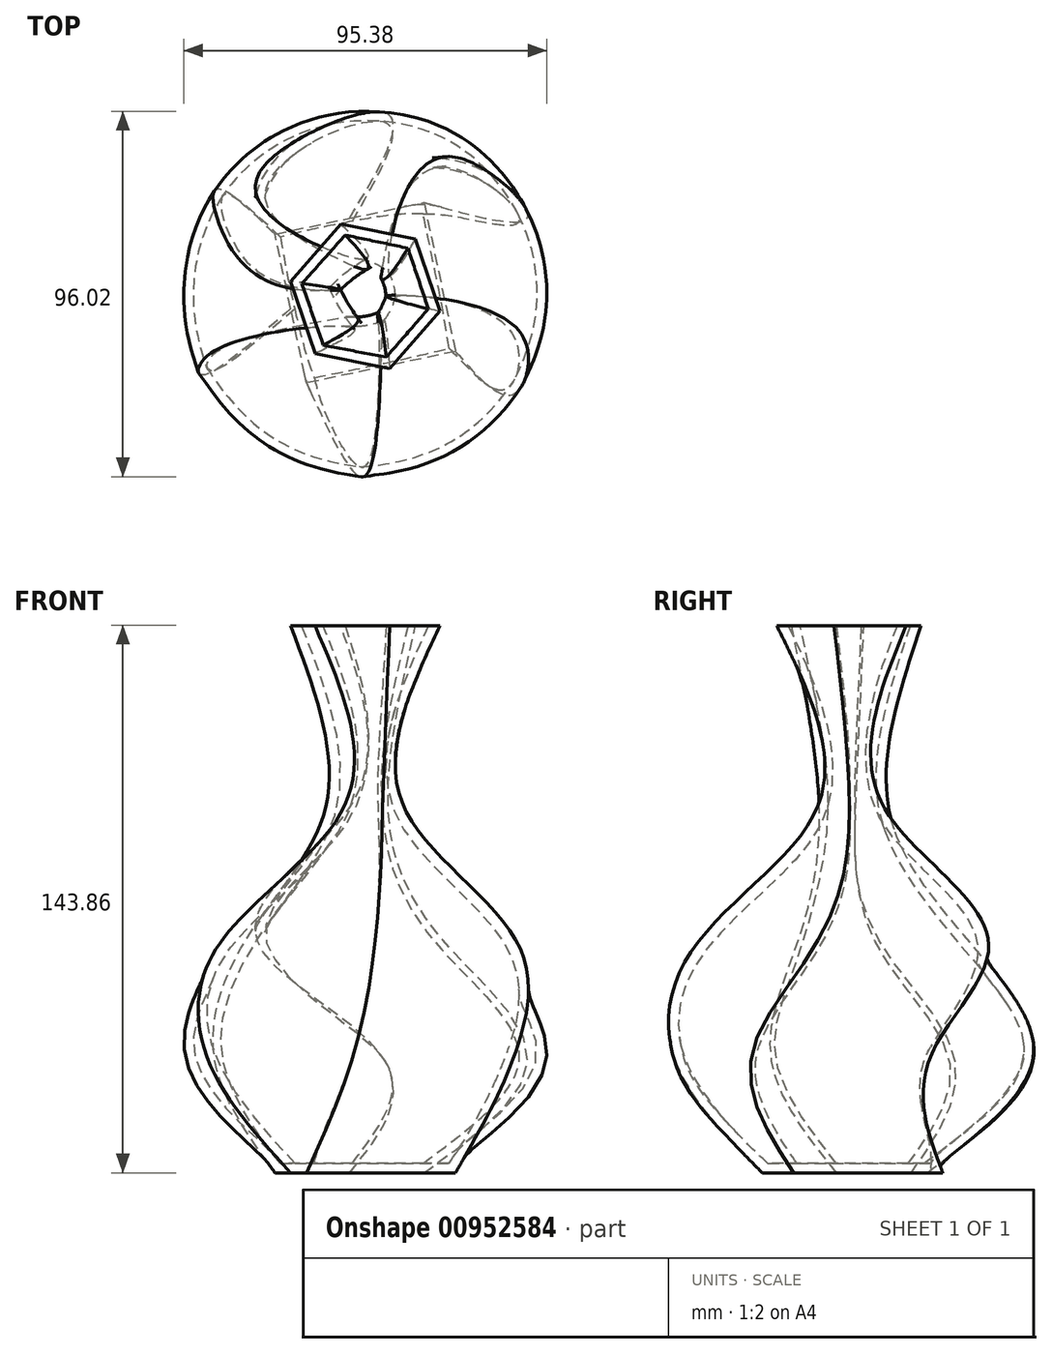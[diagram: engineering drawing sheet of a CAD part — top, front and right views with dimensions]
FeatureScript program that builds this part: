
annotation { "Feature Type Name" : "Feature", "Feature Type Description" : "" }
export const myFeature = defineFeature(function(context is Context, id is Id, definition is map)
    precondition{}
    {
        {
            var Q0;
            Q0=qCreatedBy(makeId("Top.planeOp"),FACE);
            cPlane(context, id + "F0", {"entities" : qUnion([Q0]), "cplaneType" : CPlaneType.OFFSET, "offset" : 95.2 * mm, "width" : 150 * mm, "height" : 150 * mm});
        }
        {
            var Q0;
            Q0=qCreatedBy(makeId("Top.planeOp"),FACE);
            cPlane(context, id + "F1", {"entities" : qUnion([Q0]), "cplaneType" : CPlaneType.OFFSET, "offset" : 33 * mm, "width" : 150 * mm, "height" : 150 * mm});
        }
        {
            var Q0;
            Q0=qCreatedBy(makeId("Top.planeOp"),FACE);
            var sketch = newSketch(context, id + "F2", { "sketchPlane" : qUnion([Q0])});
            skCircle(sketch, "E0.cCircle", {"center": v(0, 0) * mm, "radius": 28.28 * mm, "construction": true});
            skLineSegment(sketch, "E0.0", {"start": v(23.71, -15.42) * mm, "end": v(-15.42, -23.71) * mm});
            skLineSegment(sketch, "E0.1", {"start": v(-15.42, -23.71) * mm, "end": v(-23.71, 15.42) * mm});
            skLineSegment(sketch, "E0.2", {"start": v(-23.71, 15.42) * mm, "end": v(15.42, 23.71) * mm});
            skLineSegment(sketch, "E0.3", {"start": v(15.42, 23.71) * mm, "end": v(23.71, -15.42) * mm});
            skSolve(sketch);
        }
        {
            var Q0;
            Q0=qCreatedBy(id+"F1.planeOp",FACE);
            var sketch = newSketch(context, id + "F3", { "sketchPlane" : qUnion([Q0])});
            skCircle(sketch, "E1", {"center": v(0, 0) * mm, "radius": 47.64 * mm});
            skSolve(sketch);
        }
        {
            var Q0;
            Q0=qCreatedBy(id+"F0.planeOp",FACE);
            var sketch = newSketch(context, id + "F4", { "sketchPlane" : qUnion([Q0])});
            skCircle(sketch, "E2.cCircle", {"center": v(0, 0) * mm, "radius": 10.63 * mm, "construction": true});
            skLineSegment(sketch, "E2.0", {"start": v(4.56, -9.6) * mm, "end": v(-6.04, -8.75) * mm});
            skLineSegment(sketch, "E2.1", {"start": v(-6.04, -8.75) * mm, "end": v(-10.6, 0.85) * mm});
            skLineSegment(sketch, "E2.2", {"start": v(-10.6, 0.85) * mm, "end": v(-4.56, 9.6) * mm});
            skLineSegment(sketch, "E2.3", {"start": v(-4.56, 9.6) * mm, "end": v(6.04, 8.75) * mm});
            skLineSegment(sketch, "E2.4", {"start": v(6.04, 8.75) * mm, "end": v(10.6, -0.85) * mm});
            skLineSegment(sketch, "E2.5", {"start": v(10.6, -0.85) * mm, "end": v(4.56, -9.6) * mm});
            skSolve(sketch);
        }
        {
            var Q0;
            Q0=qCreatedBy(id+"F1.planeOp",FACE);
            cPlane(context, id + "F5", {"entities" : qUnion([Q0]), "cplaneType" : CPlaneType.OFFSET, "offset" : 110.7 * mm, "width" : 150 * mm, "height" : 150 * mm});
        }
        {
            var Q0;
            Q0=qCreatedBy(id+"F5.planeOp",FACE);
            var sketch = newSketch(context, id + "F6", { "sketchPlane" : qUnion([Q0])});
            skCircle(sketch, "E3.cCircle", {"center": v(0, -0.95) * mm, "radius": 20 * mm, "construction": true});
            skLineSegment(sketch, "E3.0", {"start": v(19.61, -4.86) * mm, "end": v(6.42, -19.89) * mm});
            skLineSegment(sketch, "E3.1", {"start": v(6.42, -19.89) * mm, "end": v(-13.2, -15.98) * mm});
            skLineSegment(sketch, "E3.2", {"start": v(-13.2, -15.98) * mm, "end": v(-19.61, 2.96) * mm});
            skLineSegment(sketch, "E3.3", {"start": v(-19.61, 2.96) * mm, "end": v(-6.42, 18) * mm});
            skLineSegment(sketch, "E3.4", {"start": v(-6.42, 18) * mm, "end": v(13.2, 14.09) * mm});
            skLineSegment(sketch, "E3.5", {"start": v(13.2, 14.09) * mm, "end": v(19.61, -4.86) * mm});
            skSolve(sketch);
        }
        {
            var Q0;
            Q0=qCreatedBy(id+"F1.planeOp",FACE);
            cPlane(context, id + "F7", {"entities" : qUnion([Q0]), "cplaneType" : CPlaneType.OFFSET, "offset" : 25 * mm, "width" : 150 * mm, "height" : 150 * mm});
        }
        {
            var Q0;
            Q0=qCreatedBy(id+"F7.planeOp",FACE);
            var sketch = newSketch(context, id + "F8", { "sketchPlane" : qUnion([Q0])});
            skCircle(sketch, "E4.cCircle", {"center": v(0, 0) * mm, "radius": 42.53 * mm, "construction": true});
            skLineSegment(sketch, "E4.0", {"start": v(41.1, -10.96) * mm, "end": v(2.28, -42.47) * mm});
            skLineSegment(sketch, "E4.1", {"start": v(2.28, -42.47) * mm, "end": v(-39.69, -15.3) * mm});
            skLineSegment(sketch, "E4.2", {"start": v(-39.69, -15.3) * mm, "end": v(-26.8, 33.02) * mm});
            skLineSegment(sketch, "E4.3", {"start": v(-26.8, 33.02) * mm, "end": v(23.12, 35.7) * mm});
            skLineSegment(sketch, "E4.4", {"start": v(23.12, 35.7) * mm, "end": v(41.1, -10.96) * mm});
            skSolve(sketch);
        }
        {
            var Q0;
            Q0=makeQuery(id+"F2.imprint","IMPRINT",FACE,{"disambiguationData":[TD([[makeQuery(id+"F2.imprint","IMPRINT",EDGE,{"derivedFrom":sQuery(id+"F2.wireOp",EDGE,"E0.0")}),-1.0]])]});
            var Q1;
            Q1=makeQuery(id+"F3.imprint","IMPRINT",FACE,{"disambiguationData":[TD([[makeQuery(id+"F3.imprint","IMPRINT",EDGE,{"derivedFrom":sQuery(id+"F3.wireOp",EDGE,"E1")}),1.0]])]});
            var Q2;
            Q2=makeQuery(id+"F8.imprint","IMPRINT",FACE,{"disambiguationData":[TD([[makeQuery(id+"F8.imprint","IMPRINT",EDGE,{"derivedFrom":sQuery(id+"F8.wireOp",EDGE,"E4.0")}),-1.0]])]});
            var Q3;
            Q3=makeQuery(id+"F4.imprint","IMPRINT",FACE,{"disambiguationData":[TD([[makeQuery(id+"F4.imprint","IMPRINT",EDGE,{"derivedFrom":sQuery(id+"F4.wireOp",EDGE,"E2.0")}),-1.0]])]});
            var Q4;
            Q4=makeQuery(id+"F6.imprint","IMPRINT",FACE,{"disambiguationData":[TD([[makeQuery(id+"F6.imprint","IMPRINT",EDGE,{"derivedFrom":sQuery(id+"F6.wireOp",EDGE,"E3.0")}),-1.0]])]});
            loft(context, id + "F9", {"sheetProfilesArray" : [{ "sheetProfileEntities" : qUnion([Q0]) }, { "sheetProfileEntities" : qUnion([Q1]) }, { "sheetProfileEntities" : qUnion([Q2]) }, { "sheetProfileEntities" : qUnion([Q3]) }, { "sheetProfileEntities" : qUnion([Q4]) }]});
        }
        {
            var Q0;
            Q0=makeQuery(id+"F9.opLoft","CAP_FACE",FACE,{"disambiguationData":[OSD([makeQuery(id+"F6.imprint","IMPRINT",FACE,{"disambiguationData":[TD([[makeQuery(id+"F6.imprint","IMPRINT",EDGE,{"derivedFrom":sQuery(id+"F6.wireOp",EDGE,"E3.0")}),-1.0]])]})])],"isStart":true});
            shell(context, id + "F10", {"entities" : qUnion([Q0]), "thickness" : 2.5 * mm});
        }
    });
